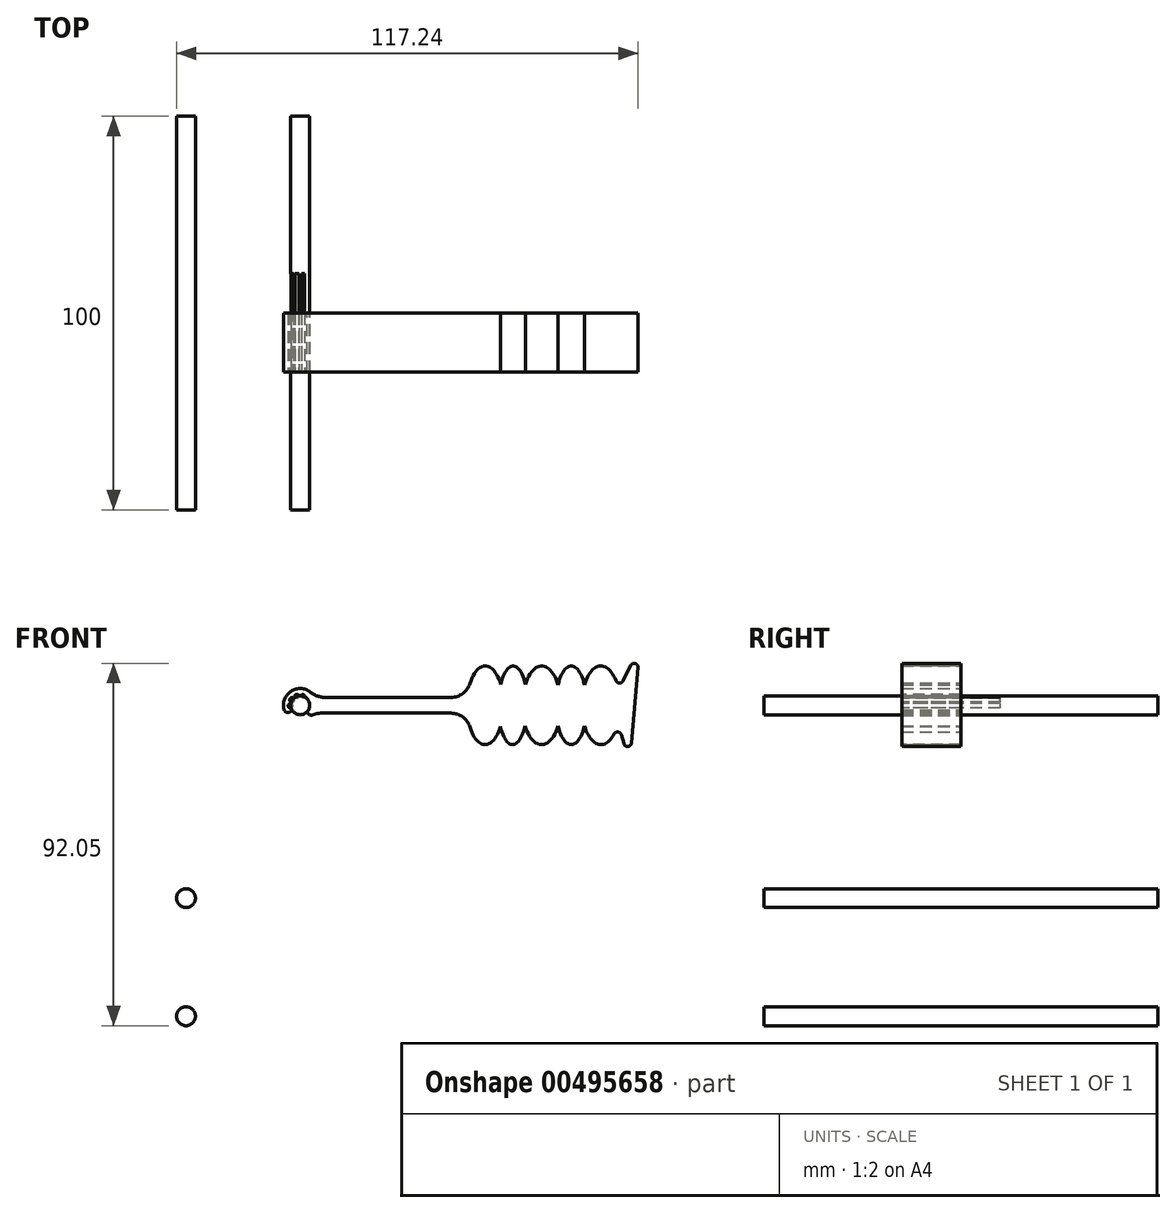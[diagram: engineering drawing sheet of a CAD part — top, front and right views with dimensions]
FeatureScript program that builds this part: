
annotation { "Feature Type Name" : "Feature", "Feature Type Description" : "" }
export const myFeature = defineFeature(function(context is Context, id is Id, definition is map)
    precondition{}
    {
        {
            var Q0;
            Q0=qCreatedBy(makeId("Front.planeOp"),FACE);
            var sketch = newSketch(context, id + "F0", { "sketchPlane" : qUnion([Q0])});
            skLineSegment(sketch, "E0", {"start": v(-29, 0) * mm, "end": v(0, 0) * mm, "construction": true});
            skLineSegment(sketch, "E1", {"start": v(0, 0) * mm, "end": v(-29, -49) * mm, "construction": true});
            skLineSegment(sketch, "E2", {"start": v(-29, -49) * mm, "end": v(-29, 0) * mm, "construction": true});
            skLineSegment(sketch, "E3", {"start": v(-29, -49) * mm, "end": v(-29, -79) * mm, "construction": true});
            skCircle(sketch, "E4", {"center": v(-29, 0) * mm, "radius": 2.4 * mm, "construction": true});
            skCircle(sketch, "E5", {"center": v(-29, -49) * mm, "radius": 2.4 * mm});
            skCircle(sketch, "E6", {"center": v(0, 0) * mm, "radius": 2.4 * mm});
            skCircle(sketch, "E7", {"center": v(-29, -79) * mm, "radius": 2.4 * mm});
            skSolve(sketch);
        }
        {
            var Q0;
            Q0 = qSketchRegion(id + "F0", true);
            extrude(context, id + "F1", {"entities" : qUnion([Q0]), "endBound" : BoundingType.SYMMETRIC, "depth" : 100 * mm});
        }
        {
            var Q0;
            Q0=qCreatedBy(makeId("Front.planeOp"),FACE);
            var sketch = newSketch(context, id + "F2", { "sketchPlane" : qUnion([Q0])});
            skLineSegment(sketch, "E8", {"start": v(0, 0) * mm, "end": v(47, 0) * mm, "construction": true});
            skArc(sketch, "E9", {"start": v(-2.17, -1.14) * mm, "mid": v(0.33, 2.43) * mm, "end": v(1.8, -1.67) * mm});
            skArc(sketch, "E10.0", {"start": v(-4.1, -1.09) * mm, "mid": v(0.49, 4.22) * mm, "end": v(3.75, -2) * mm});
            skLineSegment(sketch, "E11", {"start": v(-2.17, -1.14) * mm, "end": v(-2.26, -1.3) * mm});
            skLineSegment(sketch, "E12", {"start": v(1.8, -1.67) * mm, "end": v(2, -2.03) * mm});
            skLineSegment(sketch, "E13", {"start": v(3.75, 2) * mm, "end": v(42.45, 2) * mm});
            skLineSegment(sketch, "E14", {"start": v(86.3, 14.94) * mm, "end": v(86.3, -15.12) * mm, "construction": true});
            skLineSegment(sketch, "E15", {"start": v(80, 2) * mm, "end": v(86.3, 14.94) * mm});
            skLineSegment(sketch, "E16", {"start": v(86.3, 14.94) * mm, "end": v(83.7, -14.94) * mm});
            skLineSegment(sketch, "E17", {"start": v(83.7, -14.94) * mm, "end": v(80, -2) * mm});
            skPoint(sketch, "E18", {"position": v(85, 0) * mm});
            skLineSegment(sketch, "E19", {"start": v(80, -2) * mm, "end": v(80, 2) * mm});
            skPoint(sketch, "E20", {"position": v(80, 0) * mm});
            skLineSegment(sketch, "E21", {"start": v(47, 2) * mm, "end": v(47, 2) * mm});
            skLineSegment(sketch, "E22", {"start": v(47, 2) * mm, "end": v(47, 0) * mm});
            skLineSegment(sketch, "E23", {"start": v(80, -2) * mm, "end": v(47, -2) * mm, "construction": true});
            skPoint(sketch, "E24", {"position": v(47, 0) * mm});
            skLineSegment(sketch, "E25", {"start": v(47, -2) * mm, "end": v(42.45, -2) * mm, "construction": true});
            skLineSegment(sketch, "E26", {"start": v(51.73, 2) * mm, "end": v(80, 2) * mm, "construction": true});
            skLineSegment(sketch, "E27", {"start": v(47, 10) * mm, "end": v(103.14, 10) * mm, "construction": true});
            skEllipse(sketch, "E28", {"center": v(47, 0) * mm, "majorRadius": 10 * mm, "minorRadius": 4.64 * mm, "majorAxis": v(0, 1)});
            skLineSegment(sketch, "E29", {"start": v(47, -2) * mm, "end": v(47, 11.43) * mm, "construction": true});
            skPoint(sketch, "E30", {"position": v(47, 10) * mm});
            skFitSpline(sketch, "E31.0", {"points": [v(47.18, 8.69) * mm, v(47, 8.7) * mm, v(46.82, 8.69) * mm, v(46.54, 8.6) * mm, v(46.1, 8.33) * mm, v(45.49, 7.63) * mm, v(44.88, 6.57) * mm, v(44.36, 5.21) * mm, v(43.96, 3.6) * mm, v(43.76, 2.14) * mm, v(43.67, 0.93) * mm, v(43.65, 0) * mm, v(43.67, -0.93) * mm, v(43.76, -2.14) * mm, v(43.96, -3.6) * mm, v(44.36, -5.21) * mm, v(44.88, -6.57) * mm, v(45.49, -7.63) * mm, v(46.1, -8.33) * mm, v(46.54, -8.6) * mm, v(46.82, -8.69) * mm, v(47, -8.7) * mm, v(47.18, -8.69) * mm, v(47.46, -8.6) * mm, v(47.9, -8.33) * mm, v(48.51, -7.63) * mm, v(49.12, -6.57) * mm, v(49.64, -5.21) * mm, v(50.04, -3.6) * mm, v(50.24, -2.14) * mm, v(50.33, -0.93) * mm, v(50.35, 0) * mm, v(50.33, 0.93) * mm, v(50.24, 2.14) * mm, v(50.04, 3.6) * mm, v(49.64, 5.21) * mm, v(49.12, 6.57) * mm, v(48.51, 7.63) * mm, v(47.9, 8.33) * mm, v(47.46, 8.6) * mm, v(47.18, 8.69) * mm, v(47, 8.7) * mm, v(46.82, 8.69) * mm, v(47.18, 8.69) * mm]});
            skLineSegment(sketch, "E32", {"start": v(42.45, -2) * mm, "end": v(3.75, -2) * mm});
            skLineSegment(sketch, "E33", {"start": v(42.45, 2) * mm, "end": v(51.73, 2) * mm, "construction": true});
            skEllipse(sketch, "E34", {"center": v(54.04, 0) * mm, "majorRadius": 10 * mm, "minorRadius": 3.7 * mm, "majorAxis": v(0, 1)});
            skFitSpline(sketch, "E35.0", {"points": [v(54.13, 8.7) * mm, v(54.11, 8.7) * mm, v(54.1, 8.7) * mm, v(54.02, 8.67) * mm, v(53.87, 8.58) * mm, v(53.6, 8.33) * mm, v(53.18, 7.75) * mm, v(52.69, 6.68) * mm, v(52.25, 5.3) * mm, v(51.92, 3.67) * mm, v(51.74, 2.19) * mm, v(51.66, 0.96) * mm, v(51.64, 0.02) * mm, v(51.65, -0.92) * mm, v(51.7, -2.15) * mm, v(51.86, -3.63) * mm, v(52.17, -5.27) * mm, v(52.58, -6.66) * mm, v(53.06, -7.74) * mm, v(53.47, -8.32) * mm, v(53.73, -8.58) * mm, v(53.88, -8.67) * mm, v(53.95, -8.7) * mm, v(53.97, -8.7) * mm, v(54, -8.7) * mm, v(54.07, -8.67) * mm, v(54.21, -8.58) * mm, v(54.48, -8.33) * mm, v(54.9, -7.75) * mm, v(55.4, -6.68) * mm, v(55.83, -5.3) * mm, v(56.17, -3.67) * mm, v(56.34, -2.19) * mm, v(56.42, -0.96) * mm, v(56.45, -0.02) * mm, v(56.44, 0.92) * mm, v(56.38, 2.15) * mm, v(56.22, 3.63) * mm, v(55.91, 5.27) * mm, v(55.5, 6.66) * mm, v(55.02, 7.74) * mm, v(54.61, 8.32) * mm, v(54.35, 8.58) * mm, v(54.2, 8.67) * mm, v(54.13, 8.7) * mm, v(54.11, 8.7) * mm, v(54.1, 8.7) * mm, v(54.13, 8.7) * mm]});
            skEllipse(sketch, "E36", {"center": v(61.34, 0) * mm, "majorRadius": 10 * mm, "minorRadius": 4.9 * mm, "majorAxis": v(0, 1)});
            skFitSpline(sketch, "E37.0", {"points": [v(61.56, 8.69) * mm, v(61.34, 8.7) * mm, v(61.12, 8.69) * mm, v(60.8, 8.6) * mm, v(60.32, 8.3) * mm, v(59.66, 7.6) * mm, v(59.03, 6.55) * mm, v(58.48, 5.2) * mm, v(58.06, 3.6) * mm, v(57.84, 2.13) * mm, v(57.76, 0.92) * mm, v(57.73, 0) * mm, v(57.76, -0.92) * mm, v(57.84, -2.13) * mm, v(58.06, -3.6) * mm, v(58.48, -5.2) * mm, v(59.03, -6.55) * mm, v(59.66, -7.6) * mm, v(60.32, -8.3) * mm, v(60.8, -8.6) * mm, v(61.12, -8.69) * mm, v(61.34, -8.7) * mm, v(61.56, -8.69) * mm, v(61.88, -8.6) * mm, v(62.36, -8.3) * mm, v(63.01, -7.6) * mm, v(63.65, -6.55) * mm, v(64.2, -5.2) * mm, v(64.61, -3.6) * mm, v(64.83, -2.13) * mm, v(64.92, -0.92) * mm, v(64.94, 0) * mm, v(64.92, 0.92) * mm, v(64.83, 2.13) * mm, v(64.61, 3.6) * mm, v(64.2, 5.2) * mm, v(63.65, 6.55) * mm, v(63.01, 7.6) * mm, v(62.36, 8.3) * mm, v(61.88, 8.6) * mm, v(61.56, 8.69) * mm, v(61.34, 8.7) * mm, v(61.12, 8.69) * mm, v(61.56, 8.69) * mm]});
            skEllipse(sketch, "E38", {"center": v(68.87, 0) * mm, "majorRadius": 10 * mm, "minorRadius": 3.94 * mm, "majorAxis": v(0, 1)});
            skFitSpline(sketch, "E39.0", {"points": [v(68.93, 8.7) * mm, v(68.87, 8.7) * mm, v(68.8, 8.7) * mm, v(68.7, 8.66) * mm, v(68.53, 8.55) * mm, v(68.24, 8.3) * mm, v(67.8, 7.72) * mm, v(67.29, 6.65) * mm, v(66.84, 5.27) * mm, v(66.5, 3.64) * mm, v(66.32, 2.16) * mm, v(66.25, 0.94) * mm, v(66.23, 0) * mm, v(66.25, -0.94) * mm, v(66.32, -2.16) * mm, v(66.5, -3.64) * mm, v(66.84, -5.27) * mm, v(67.29, -6.65) * mm, v(67.8, -7.72) * mm, v(68.24, -8.3) * mm, v(68.53, -8.55) * mm, v(68.7, -8.66) * mm, v(68.8, -8.7) * mm, v(68.87, -8.7) * mm, v(68.93, -8.7) * mm, v(69.04, -8.66) * mm, v(69.21, -8.55) * mm, v(69.5, -8.3) * mm, v(69.94, -7.72) * mm, v(70.46, -6.65) * mm, v(70.9, -5.27) * mm, v(71.25, -3.64) * mm, v(71.42, -2.16) * mm, v(71.5, -0.94) * mm, v(71.51, 0) * mm, v(71.5, 0.94) * mm, v(71.42, 2.16) * mm, v(71.25, 3.64) * mm, v(70.9, 5.27) * mm, v(70.46, 6.65) * mm, v(69.94, 7.72) * mm, v(69.5, 8.3) * mm, v(69.21, 8.55) * mm, v(69.04, 8.66) * mm, v(68.93, 8.7) * mm, v(68.87, 8.7) * mm, v(68.8, 8.7) * mm, v(68.93, 8.7) * mm]});
            skEllipse(sketch, "E40", {"center": v(76.4, 0) * mm, "majorRadius": 10 * mm, "minorRadius": 4.9 * mm, "majorAxis": v(0, 1)});
            skFitSpline(sketch, "E41.0", {"points": [v(76.62, 8.69) * mm, v(76.4, 8.7) * mm, v(76.18, 8.69) * mm, v(75.86, 8.6) * mm, v(75.38, 8.3) * mm, v(74.73, 7.6) * mm, v(74.1, 6.55) * mm, v(73.55, 5.2) * mm, v(73.13, 3.6) * mm, v(72.91, 2.13) * mm, v(72.82, 0.92) * mm, v(72.8, 0) * mm, v(72.82, -0.92) * mm, v(72.91, -2.13) * mm, v(73.13, -3.6) * mm, v(73.55, -5.2) * mm, v(74.1, -6.55) * mm, v(74.73, -7.6) * mm, v(75.38, -8.3) * mm, v(75.86, -8.6) * mm, v(76.18, -8.69) * mm, v(76.4, -8.7) * mm, v(76.62, -8.69) * mm, v(76.94, -8.6) * mm, v(77.42, -8.3) * mm, v(78.08, -7.6) * mm, v(78.71, -6.55) * mm, v(79.26, -5.2) * mm, v(79.68, -3.6) * mm, v(79.9, -2.13) * mm, v(79.99, -0.92) * mm, v(80, 0) * mm, v(79.99, 0.92) * mm, v(79.9, 2.13) * mm, v(79.68, 3.6) * mm, v(79.26, 5.2) * mm, v(78.71, 6.55) * mm, v(78.08, 7.6) * mm, v(77.42, 8.3) * mm, v(76.94, 8.6) * mm, v(76.62, 8.69) * mm, v(76.4, 8.7) * mm, v(76.18, 8.69) * mm, v(76.62, 8.69) * mm]});
            skPoint(sketch, "E42", {"position": v(54.11, 10) * mm});
            skPoint(sketch, "E43", {"position": v(61.34, 10) * mm});
            skPoint(sketch, "E44", {"position": v(68.87, 10) * mm});
            skPoint(sketch, "E45", {"position": v(70.61, 10) * mm});
            skPoint(sketch, "E46", {"position": v(76.4, 10) * mm});
            skLineSegment(sketch, "E47", {"start": v(44.18, 8.7) * mm, "end": v(91.15, 8.7) * mm, "construction": true});
            skPoint(sketch, "E48", {"position": v(47, 8.7) * mm});
            skLineSegment(sketch, "E49", {"start": v(54.04, 0) * mm, "end": v(61.34, 0) * mm, "construction": true});
            skLineSegment(sketch, "E50", {"start": v(61.34, 0) * mm, "end": v(68.87, 0) * mm, "construction": true});
            skLineSegment(sketch, "E51", {"start": v(68.87, 0) * mm, "end": v(76.4, 0) * mm, "construction": true});
            skLineSegment(sketch, "E52", {"start": v(76.4, 0) * mm, "end": v(86.3, 0) * mm, "construction": true});
            skLineSegment(sketch, "E53", {"start": v(47, 0) * mm, "end": v(47, -2) * mm});
            skLineSegment(sketch, "E54", {"start": v(47, 0) * mm, "end": v(54.04, 0) * mm, "construction": true});
            skPoint(sketch, "E55.visualSharp", {"position": v(-3.1, -2.9) * mm});
            skArc(sketch, "E55.filletArc", {"start": v(-4.1, -1.09) * mm, "mid": v(-3.26, -1.83) * mm, "end": v(-2.26, -1.3) * mm});
            skPoint(sketch, "E56.visualSharp", {"position": v(2.72, -3.27) * mm});
            skArc(sketch, "E56.filletArc", {"start": v(2, -2.03) * mm, "mid": v(2.88, -2.53) * mm, "end": v(3.75, -2) * mm});
            skSolve(sketch);
        }
        {
            var Q0;
            Q0 = qSketchRegion(id + "F2", true);
            extrude(context, id + "F3", {"entities" : qUnion([Q0]), "offsetDistance" : 25 * mm, "depth" : 15 * mm});
        }
        {
            var Q0;
            Q0=makeQuery(id+"F3.opExtrude","SWEPT_EDGE",EDGE,{"disambiguationData":[OSD([sQuery(id+"F2.wireOp",EDGE,"E10.0"),sQuery(id+"F2.wireOp",EDGE,"E13")])]});
            fillet(context, id + "F4", {"entities" : qUnion([Q0]), "radius" : 6 * mm, "tangentPropagation" : true, "allowEdgeOverflow" : false});
        }
        {
            var Q0;
            Q0=makeQuery(id+"F3.opExtrude","SWEPT_EDGE",EDGE,{"disambiguationData":[OSD([sQuery(id+"F2.wireOp",EDGE,"E13"),sQuery(id+"F2.wireOp",EDGE,"E28")])]});
            fillet(context, id + "F5", {"entities" : qUnion([Q0]), "radius" : 5 * mm, "tangentPropagation" : true, "allowEdgeOverflow" : false});
        }
        {
            var Q0;
            Q0=makeQuery(id+"F3.opExtrude","SWEPT_EDGE",EDGE,{"disambiguationData":[OSD([sQuery(id+"F2.wireOp",EDGE,"E28"),sQuery(id+"F2.wireOp",EDGE,"E32")])]});
            fillet(context, id + "F6", {"entities" : qUnion([Q0]), "radius" : 5 * mm, "tangentPropagation" : true, "allowEdgeOverflow" : false});
        }
        {
            var Q0;
            Q0=makeQuery(id+"F3.opExtrude","SWEPT_EDGE",EDGE,{"disambiguationData":[OSD([sQuery(id+"F2.wireOp",EDGE,"E15"),sQuery(id+"F2.wireOp",EDGE,"E40")])]});
            fillet(context, id + "F7", {"entities" : qUnion([Q0]), "radius" : 1 * mm, "tangentPropagation" : true, "allowEdgeOverflow" : false});
        }
        {
            var Q0;
            Q0=makeQuery(id+"F3.opExtrude","SWEPT_EDGE",EDGE,{"disambiguationData":[OSD([sQuery(id+"F2.wireOp",EDGE,"E15"),sQuery(id+"F2.wireOp",EDGE,"E16")])]});
            fillet(context, id + "F8", {"entities" : qUnion([Q0]), "radius" : 1 * mm, "tangentPropagation" : true, "allowEdgeOverflow" : false});
        }
        {
            var Q0;
            Q0=makeQuery(id+"F3.opExtrude","SWEPT_EDGE",EDGE,{"disambiguationData":[OSD([sQuery(id+"F2.wireOp",EDGE,"E16"),sQuery(id+"F2.wireOp",EDGE,"E17")])]});
            fillet(context, id + "F9", {"entities" : qUnion([Q0]), "radius" : 1 * mm, "tangentPropagation" : true, "allowEdgeOverflow" : false});
        }
        {
            var Q0;
            Q0=makeQuery(id+"F3.opExtrude","SWEPT_EDGE",EDGE,{"disambiguationData":[OSD([sQuery(id+"F2.wireOp",EDGE,"E17"),sQuery(id+"F2.wireOp",EDGE,"E40")])]});
            fillet(context, id + "F10", {"entities" : qUnion([Q0]), "radius" : 1 * mm, "tangentPropagation" : true, "allowEdgeOverflow" : false});
        }
        {
            var Q0;
            Q0=makeQuery(id+"F3.opExtrude","SWEPT_EDGE",EDGE,{"disambiguationData":[OSD([sQuery(id+"F2.wireOp",EDGE,"E10.0"),sQuery(id+"F2.wireOp",EDGE,"E32")])]});
            fillet(context, id + "F11", {"entities" : qUnion([Q0]), "radius" : 5 * mm, "tangentPropagation" : true, "allowEdgeOverflow" : false});
        }
        {
            var Q0;
            Q0=makeQuery(id+"F3.opExtrude","CAP_FACE",FACE,{"disambiguationData":[OSD([sQuery(id+"F2.wireOp",EDGE,"E9"),sQuery(id+"F2.wireOp",EDGE,"E10.0"),sQuery(id+"F2.wireOp",EDGE,"E11"),sQuery(id+"F2.wireOp",EDGE,"E12"),sQuery(id+"F2.wireOp",EDGE,"E13"),sQuery(id+"F2.wireOp",EDGE,"E15"),sQuery(id+"F2.wireOp",EDGE,"E16"),sQuery(id+"F2.wireOp",EDGE,"E17"),sQuery(id+"F2.wireOp",EDGE,"E28"),sQuery(id+"F2.wireOp",EDGE,"E31.0"),sQuery(id+"F2.wireOp",EDGE,"E32"),sQuery(id+"F2.wireOp",EDGE,"E34"),sQuery(id+"F2.wireOp",EDGE,"E35.0"),sQuery(id+"F2.wireOp",EDGE,"E36"),sQuery(id+"F2.wireOp",EDGE,"E37.0"),sQuery(id+"F2.wireOp",EDGE,"E38"),sQuery(id+"F2.wireOp",EDGE,"E39.0"),sQuery(id+"F2.wireOp",EDGE,"E40"),sQuery(id+"F2.wireOp",EDGE,"E41.0"),sQuery(id+"F2.wireOp",EDGE,"E55.filletArc"),sQuery(id+"F2.wireOp",EDGE,"E56.filletArc")])],"isStart":false});
            var sketch = newSketch(context, id + "F12", { "sketchPlane" : qUnion([Q0])});
            skArc(sketch, "E57.0", {"start": v(-2.17, -1.14) * mm, "mid": v(0.33, 2.43) * mm, "end": v(1.8, -1.67) * mm});
            skLineSegment(sketch, "E58.anchor1", {"start": v(0, 0) * mm, "end": v(-2.45, -0.14) * mm, "construction": true});
            skPoint(sketch, "E59", {"position": v(-2.45, -0.14) * mm});
            skPoint(sketch, "E60.1.0", {"position": v(-2.04, 1.35) * mm});
            skPoint(sketch, "E60.2.0", {"position": v(-0.83, 2.3) * mm});
            skPoint(sketch, "E60.3.0", {"position": v(0.7, 2.35) * mm});
            skLineSegment(sketch, "E60.anchor2", {"start": v(0, 0) * mm, "end": v(0.7, 2.35) * mm, "construction": true});
            skCircle(sketch, "E61", {"center": v(-2.45, -0.14) * mm, "radius": 0.6 * mm});
            skCircle(sketch, "E62", {"center": v(-2.04, 1.35) * mm, "radius": 0.6 * mm});
            skCircle(sketch, "E63", {"center": v(-0.83, 2.3) * mm, "radius": 0.5 * mm});
            skCircle(sketch, "E64", {"center": v(0.7, 2.35) * mm, "radius": 0.4 * mm});
            skSolve(sketch);
        }
        {
            var Q0;
            Q0 = qSketchRegion(id + "F12", true);
            extrude(context, id + "F13", {"entities" : qUnion([Q0]), "operationType" : NewBodyOperationType.REMOVE, "oppositeDirection" : true, "depth" : 25 * mm, "offsetDistance" : 25 * mm});
        }
    });
